# Revit family: 519-21
name_source: partatom
category: Plumbing Fixtures
revit_build: Autodesk Revit Architecture 2012 (Build: 20110309_2315(x64)
units: mm (PartAtom-declared; Revit-internal decimal feet)

## types (1)
- 519-21
    Assembly Code = D2010
    Blue Headpart only = S-21-1CLOCK
    Blue headpart complete = S-21-CLOCK
    CW Connection = Yes
    CWFU = 0
    Cost = 0 $
    Default Elevation = 0' - 0"
    Description = Elbow action. Bibtap + hose + handspray + wall holder 1/4 turn. 1/2"BSP MI
    HW Connection = Yes
    HWFU = 0
    Keynote = Ideal for medical, mortuary, kitchen and industrial installations
    Manufacturer = COBRA
    Material = Chrome - Polished
    Model = 519-21
    Range = Medical Elbow Action
    Trigger spray and tube = 27824SP
    Type Comments = SANS 226 TYPE 2
    URL = http://www.cobra.co.za
    Vent Connection = No
    WFU = 0
    Wall mounted handshower holder = 28020
    Waste Connection = No

## geometry (parser evidence)
native form markers: Blend x3
no freeform markers — native parametric forms only
